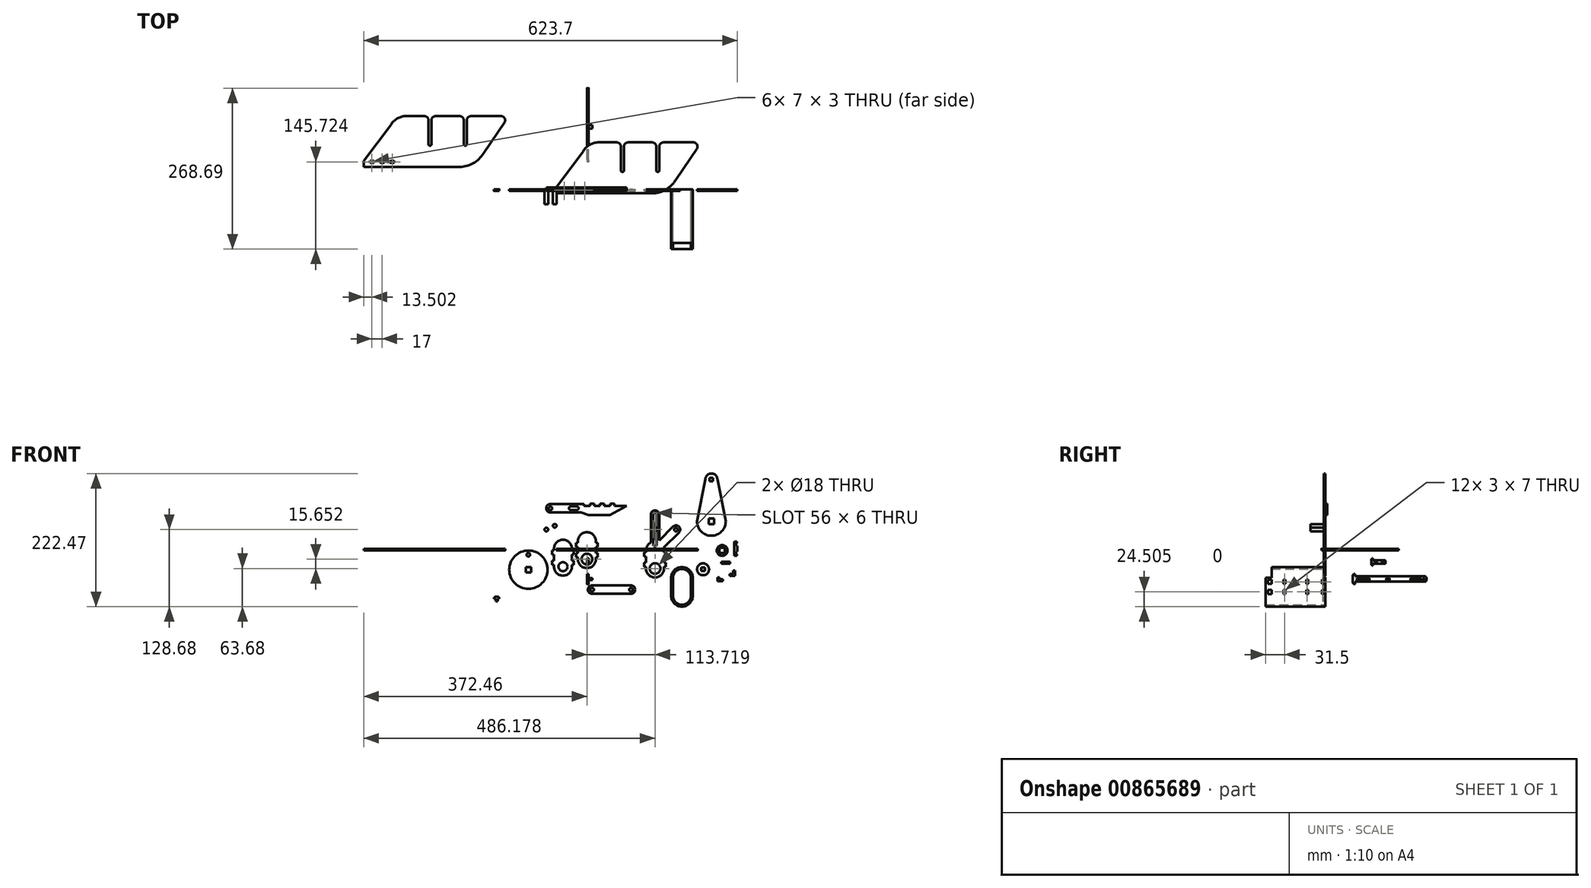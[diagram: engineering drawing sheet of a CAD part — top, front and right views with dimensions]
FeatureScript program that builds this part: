
annotation { "Feature Type Name" : "Feature", "Feature Type Description" : "" }
export const myFeature = defineFeature(function(context is Context, id is Id, definition is map)
    precondition{}
    {
        {
            var Q0;
            Q0=qCreatedBy(makeId("Front.planeOp"),FACE);
            var sketch = newSketch(context, id + "F0", { "sketchPlane" : qUnion([Q0])});
            skLineSegment(sketch, "E0.bottom", {"start": v(-26.86, 73.6) * mm, "end": v(-16.93, 73.6) * mm});
            skLineSegment(sketch, "E0.top", {"start": v(-26.86, 67.6) * mm, "end": v(-16.93, 67.6) * mm});
            skLineSegment(sketch, "E0.right", {"start": v(-16.93, 73.6) * mm, "end": v(-16.93, 67.6) * mm, "construction": true});
            skArc(sketch, "E1", {"start": v(-26.86, 73.6) * mm, "mid": v(-29.93, 70.6) * mm, "end": v(-26.86, 67.6) * mm});
            skArc(sketch, "E2", {"start": v(-16.93, 67.6) * mm, "mid": v(-13.93, 70.6) * mm, "end": v(-16.93, 73.6) * mm});
            skLineSegment(sketch, "E3.bottom", {"start": v(-60.93, 77.6) * mm, "end": v(-9.93, 77.6) * mm});
            skLineSegment(sketch, "E3.top", {"start": v(-60.93, 63.6) * mm, "end": v(-9.93, 63.6) * mm});
            skLineSegment(sketch, "E3.right", {"start": v(-9.93, 77.6) * mm, "end": v(-9.93, 63.6) * mm, "construction": true});
            skArc(sketch, "E4", {"start": v(-60.93, 77.6) * mm, "mid": v(-67.93, 70.6) * mm, "end": v(-60.93, 63.6) * mm});
            skCircle(sketch, "E5", {"center": v(-60.93, 70.6) * mm, "radius": 3 * mm});
            skLineSegment(sketch, "E6", {"start": v(3.07, 59.6) * mm, "end": v(38.07, 59.6) * mm});
            skLineSegment(sketch, "E7", {"start": v(38.07, 59.6) * mm, "end": v(66.07, 74.6) * mm});
            skLineSegment(sketch, "E8", {"start": v(66.07, 74.6) * mm, "end": v(46.07, 74.6) * mm});
            skLineSegment(sketch, "E9", {"start": v(46.07, 74.6) * mm, "end": v(46.07, 78.6) * mm});
            skLineSegment(sketch, "E10", {"start": v(46.07, 78.6) * mm, "end": v(39.07, 78.6) * mm});
            skLineSegment(sketch, "E11", {"start": v(39.07, 78.6) * mm, "end": v(39.07, 74.6) * mm});
            skLineSegment(sketch, "E12", {"start": v(39.07, 74.6) * mm, "end": v(29.07, 74.6) * mm});
            skLineSegment(sketch, "E13", {"start": v(29.07, 74.6) * mm, "end": v(29.07, 78.6) * mm});
            skLineSegment(sketch, "E14", {"start": v(29.07, 78.6) * mm, "end": v(22.07, 78.6) * mm});
            skLineSegment(sketch, "E15", {"start": v(22.07, 78.6) * mm, "end": v(22.07, 74.6) * mm});
            skLineSegment(sketch, "E16", {"start": v(22.07, 74.6) * mm, "end": v(12.07, 74.6) * mm});
            skLineSegment(sketch, "E17", {"start": v(12.07, 74.6) * mm, "end": v(12.07, 78.6) * mm});
            skLineSegment(sketch, "E18", {"start": v(12.07, 78.6) * mm, "end": v(5.07, 78.6) * mm});
            skLineSegment(sketch, "E19", {"start": v(5.07, 78.6) * mm, "end": v(5.07, 74.6) * mm});
            skLineSegment(sketch, "E20", {"start": v(12.07, 78.6) * mm, "end": v(39.07, 78.6) * mm, "construction": true});
            skLineSegment(sketch, "E21", {"start": v(22.07, 74.6) * mm, "end": v(29.07, 74.6) * mm, "construction": true});
            skLineSegment(sketch, "E22", {"start": v(39.07, 74.6) * mm, "end": v(46.07, 74.6) * mm, "construction": true});
            skLineSegment(sketch, "E23", {"start": v(-9.93, 63.6) * mm, "end": v(3.07, 59.6) * mm});
            skLineSegment(sketch, "E24", {"start": v(-9.93, 77.6) * mm, "end": v(-4.93, 77.6) * mm});
            skLineSegment(sketch, "E25", {"start": v(-4.93, 77.6) * mm, "end": v(-4.93, 74.6) * mm});
            skLineSegment(sketch, "E26", {"start": v(-4.93, 74.6) * mm, "end": v(5.07, 74.6) * mm});
            skLineSegment(sketch, "E27", {"start": v(-60.93, 77.6) * mm, "end": v(-60.93, 63.6) * mm, "construction": true});
            skLineSegment(sketch, "E28", {"start": v(-26.86, 73.6) * mm, "end": v(-26.86, 67.6) * mm, "construction": true});
            skSolve(sketch);
        }
        {
            var Q0;
            Q0=qCreatedBy(makeId("Front.planeOp"),FACE);
            var sketch = newSketch(context, id + "F1", { "sketchPlane" : qUnion([Q0])});
            skLineSegment(sketch, "E29", {"start": v(-54.91, 3) * mm, "end": v(-24.91, 3) * mm, "construction": true});
            skCircle(sketch, "E30", {"center": v(-39.91, -27) * mm, "radius": 7.5 * mm});
            skLineSegment(sketch, "E31", {"start": v(-24.91, 3) * mm, "end": v(-24.91, 0) * mm});
            skLineSegment(sketch, "E32", {"start": v(-21.91, 0) * mm, "end": v(-24.91, 0) * mm});
            skLineSegment(sketch, "E33", {"start": v(-21.91, 0) * mm, "end": v(-21.91, -7) * mm});
            skLineSegment(sketch, "E34", {"start": v(-24.91, -7) * mm, "end": v(-21.91, -7) * mm});
            skLineSegment(sketch, "E35", {"start": v(-24.91, -7) * mm, "end": v(-24.91, -17) * mm});
            skLineSegment(sketch, "E36", {"start": v(-21.91, -17) * mm, "end": v(-24.91, -17) * mm});
            skLineSegment(sketch, "E37", {"start": v(-21.91, -17) * mm, "end": v(-21.91, -24) * mm});
            skLineSegment(sketch, "E38", {"start": v(-24.91, -24) * mm, "end": v(-21.91, -24) * mm});
            skLineSegment(sketch, "E39", {"start": v(-24.91, -24) * mm, "end": v(-24.91, -27) * mm});
            skLineSegment(sketch, "E40", {"start": v(-54.91, 3) * mm, "end": v(-54.91, 0) * mm});
            skLineSegment(sketch, "E41", {"start": v(-57.91, 0) * mm, "end": v(-54.91, 0) * mm});
            skLineSegment(sketch, "E42", {"start": v(-57.91, 0) * mm, "end": v(-57.91, -7) * mm});
            skLineSegment(sketch, "E43", {"start": v(-54.91, -7) * mm, "end": v(-57.91, -7) * mm});
            skLineSegment(sketch, "E44", {"start": v(-54.91, -7) * mm, "end": v(-54.91, -17) * mm});
            skLineSegment(sketch, "E45", {"start": v(-57.91, -17) * mm, "end": v(-54.91, -17) * mm});
            skLineSegment(sketch, "E46", {"start": v(-57.91, -17) * mm, "end": v(-57.91, -24) * mm});
            skLineSegment(sketch, "E47", {"start": v(-54.91, -24) * mm, "end": v(-57.91, -24) * mm});
            skLineSegment(sketch, "E48", {"start": v(-54.91, -24) * mm, "end": v(-54.91, -27) * mm});
            skLineSegment(sketch, "E49", {"start": v(-54.91, -27) * mm, "end": v(-24.91, -27) * mm, "construction": true});
            skArc(sketch, "E50", {"start": v(-24.91, 3) * mm, "mid": v(-39.91, 18) * mm, "end": v(-54.91, 3) * mm});
            skArc(sketch, "E51", {"start": v(-54.91, -27) * mm, "mid": v(-39.91, -42) * mm, "end": v(-24.91, -27) * mm});
            skSolve(sketch);
        }
        {
            var Q0;
            Q0=qCreatedBy(makeId("Top.planeOp"),FACE);
            var sketch = newSketch(context, id + "F2", { "sketchPlane" : qUnion([Q0])});
            skLineSegment(sketch, "E52", {"start": v(-51.21, -6.8) * mm, "end": v(108.79, -6.8) * mm});
            skLineSegment(sketch, "E53", {"start": v(148.63, 16.2) * mm, "end": v(183.83, 67.7) * mm});
            skLineSegment(sketch, "E54", {"start": v(-6.21, 63.2) * mm, "end": v(-51.21, 3.2) * mm});
            skLineSegment(sketch, "E55", {"start": v(-51.21, 3.2) * mm, "end": v(-51.21, -6.8) * mm});
            skArc(sketch, "E56", {"start": v(108.79, -6.8) * mm, "mid": v(131.79, -0.64) * mm, "end": v(148.63, 16.2) * mm});
            skLineSegment(sketch, "E57", {"start": v(-41.21, -2.8) * mm, "end": v(-0.21, -2.8) * mm, "construction": true});
            skLineSegment(sketch, "E58", {"start": v(-0.21, -2.8) * mm, "end": v(-0.21, -6.8) * mm, "construction": true});
            skLineSegment(sketch, "E59", {"start": v(-0.21, -2.8) * mm, "end": v(-0.21, 3.2) * mm, "construction": true});
            skLineSegment(sketch, "E60", {"start": v(-0.21, 3.2) * mm, "end": v(-41.21, 3.2) * mm, "construction": true});
            skLineSegment(sketch, "E61", {"start": v(-41.21, 3.2) * mm, "end": v(-41.21, -2.8) * mm, "construction": true});
            skLineSegment(sketch, "E62", {"start": v(-51.21, 3.2) * mm, "end": v(-41.21, 3.2) * mm, "construction": true});
            skLineSegment(sketch, "E63", {"start": v(-51.21, 3.2) * mm, "end": v(-51.21, -96.8) * mm, "construction": true});
            skLineSegment(sketch, "E64", {"start": v(-51.21, -96.8) * mm, "end": v(188.79, -96.8) * mm, "construction": true});
            skLineSegment(sketch, "E65", {"start": v(188.79, -96.8) * mm, "end": v(188.79, 73.46) * mm, "construction": true});
            skLineSegment(sketch, "E66.bottom", {"start": v(-41.21, -2.8) * mm, "end": v(-34.21, -2.8) * mm});
            skLineSegment(sketch, "E66.top", {"start": v(-41.21, 0.2) * mm, "end": v(-34.21, 0.2) * mm});
            skLineSegment(sketch, "E66.left", {"start": v(-41.21, -2.8) * mm, "end": v(-41.21, 0.2) * mm});
            skLineSegment(sketch, "E66.right", {"start": v(-34.21, -2.8) * mm, "end": v(-34.21, 0.2) * mm});
            skLineSegment(sketch, "E67.bottom", {"start": v(-24.21, -2.8) * mm, "end": v(-17.21, -2.8) * mm});
            skLineSegment(sketch, "E67.top", {"start": v(-24.21, 0.2) * mm, "end": v(-17.21, 0.2) * mm});
            skLineSegment(sketch, "E67.left", {"start": v(-24.21, -2.8) * mm, "end": v(-24.21, 0.2) * mm});
            skLineSegment(sketch, "E67.right", {"start": v(-17.21, -2.8) * mm, "end": v(-17.21, 0.2) * mm});
            skLineSegment(sketch, "E68.bottom", {"start": v(-0.21, -2.8) * mm, "end": v(-7.21, -2.8) * mm});
            skLineSegment(sketch, "E68.top", {"start": v(-0.21, 0.2) * mm, "end": v(-7.21, 0.2) * mm});
            skLineSegment(sketch, "E68.left", {"start": v(-0.21, -2.8) * mm, "end": v(-0.21, 0.2) * mm});
            skLineSegment(sketch, "E68.right", {"start": v(-7.21, -2.8) * mm, "end": v(-7.21, 0.2) * mm});
            skLineSegment(sketch, "E69", {"start": v(108.79, 39.2) * mm, "end": v(108.79, -6.8) * mm, "construction": true});
            skLineSegment(sketch, "E70", {"start": v(108.79, 39.2) * mm, "end": v(148.63, 16.2) * mm, "construction": true});
            skArc(sketch, "E71", {"start": v(183.83, 67.7) * mm, "mid": v(183.83, 74.7) * mm, "end": v(177.77, 78.2) * mm});
            skLineSegment(sketch, "E72", {"start": v(177.77, 78.2) * mm, "end": v(177.77, 71.2) * mm, "construction": true});
            skLineSegment(sketch, "E73", {"start": v(183.83, 67.7) * mm, "end": v(177.77, 71.2) * mm, "construction": true});
            skLineSegment(sketch, "E74", {"start": v(177.77, 78.2) * mm, "end": v(127.77, 78.2) * mm});
            skLineSegment(sketch, "E75", {"start": v(120.77, 71.2) * mm, "end": v(120.77, 31.2) * mm});
            skLineSegment(sketch, "E76", {"start": v(115.77, 71.2) * mm, "end": v(115.77, 31.2) * mm});
            skLineSegment(sketch, "E77", {"start": v(61.77, 71.2) * mm, "end": v(61.77, 31.2) * mm});
            skLineSegment(sketch, "E78", {"start": v(56.77, 71.2) * mm, "end": v(56.77, 31.2) * mm});
            skLineSegment(sketch, "E79", {"start": v(19.77, 78.2) * mm, "end": v(49.77, 78.2) * mm});
            skLineSegment(sketch, "E80", {"start": v(68.77, 78.2) * mm, "end": v(108.77, 78.2) * mm});
            skArc(sketch, "E81", {"start": v(127.77, 78.2) * mm, "mid": v(122.82, 76.15) * mm, "end": v(120.77, 71.2) * mm});
            skArc(sketch, "E82", {"start": v(115.77, 71.2) * mm, "mid": v(113.72, 76.15) * mm, "end": v(108.77, 78.2) * mm});
            skArc(sketch, "E83", {"start": v(115.77, 31.2) * mm, "mid": v(118.27, 28.7) * mm, "end": v(120.77, 31.2) * mm});
            skArc(sketch, "E84", {"start": v(68.77, 78.2) * mm, "mid": v(63.82, 76.15) * mm, "end": v(61.77, 71.2) * mm});
            skArc(sketch, "E85", {"start": v(56.77, 71.2) * mm, "mid": v(54.72, 76.15) * mm, "end": v(49.77, 78.2) * mm});
            skArc(sketch, "E86", {"start": v(56.77, 31.2) * mm, "mid": v(59.27, 28.7) * mm, "end": v(61.77, 31.2) * mm});
            skLineSegment(sketch, "E87", {"start": v(127.77, 78.2) * mm, "end": v(127.77, 71.2) * mm, "construction": true});
            skLineSegment(sketch, "E88", {"start": v(120.77, 71.2) * mm, "end": v(127.77, 71.2) * mm, "construction": true});
            skLineSegment(sketch, "E89", {"start": v(108.77, 78.2) * mm, "end": v(108.77, 71.2) * mm, "construction": true});
            skLineSegment(sketch, "E90", {"start": v(115.77, 71.2) * mm, "end": v(108.77, 71.2) * mm, "construction": true});
            skLineSegment(sketch, "E91", {"start": v(120.77, 31.2) * mm, "end": v(115.77, 31.2) * mm, "construction": true});
            skLineSegment(sketch, "E92", {"start": v(61.77, 71.2) * mm, "end": v(68.77, 71.2) * mm, "construction": true});
            skLineSegment(sketch, "E93", {"start": v(68.77, 78.2) * mm, "end": v(68.77, 71.2) * mm, "construction": true});
            skLineSegment(sketch, "E94", {"start": v(49.77, 78.2) * mm, "end": v(49.77, 71.2) * mm, "construction": true});
            skLineSegment(sketch, "E95", {"start": v(56.77, 71.2) * mm, "end": v(49.77, 71.2) * mm, "construction": true});
            skLineSegment(sketch, "E96", {"start": v(56.77, 31.2) * mm, "end": v(61.77, 31.2) * mm, "construction": true});
            skArc(sketch, "E97", {"start": v(19.77, 78.2) * mm, "mid": v(4.77, 74.18) * mm, "end": v(-6.21, 63.2) * mm});
            skLineSegment(sketch, "E98", {"start": v(19.77, 78.2) * mm, "end": v(19.77, 48.2) * mm, "construction": true});
            skLineSegment(sketch, "E99", {"start": v(-6.21, 63.2) * mm, "end": v(19.77, 48.2) * mm, "construction": true});
            skSolve(sketch);
        }
        {
            var Q0;
            Q0=qCreatedBy(makeId("Top.planeOp"),FACE);
            var sketch = newSketch(context, id + "F3", { "sketchPlane" : qUnion([Q0])});
            skLineSegment(sketch, "E100", {"start": v(-372.46, 37.22) * mm, "end": v(-212.46, 37.22) * mm});
            skLineSegment(sketch, "E101", {"start": v(-172.62, 60.22) * mm, "end": v(-137.42, 111.72) * mm});
            skLineSegment(sketch, "E102", {"start": v(-327.46, 107.22) * mm, "end": v(-372.46, 47.22) * mm});
            skLineSegment(sketch, "E103", {"start": v(-372.46, 47.22) * mm, "end": v(-372.46, 37.22) * mm});
            skArc(sketch, "E104", {"start": v(-212.46, 37.22) * mm, "mid": v(-189.46, 43.39) * mm, "end": v(-172.62, 60.22) * mm});
            skLineSegment(sketch, "E105", {"start": v(-362.46, 41.22) * mm, "end": v(-321.46, 41.22) * mm, "construction": true});
            skLineSegment(sketch, "E106", {"start": v(-321.46, 41.22) * mm, "end": v(-321.46, 37.22) * mm, "construction": true});
            skLineSegment(sketch, "E107", {"start": v(-321.46, 41.22) * mm, "end": v(-321.46, 47.22) * mm, "construction": true});
            skLineSegment(sketch, "E108", {"start": v(-321.46, 47.22) * mm, "end": v(-362.46, 47.22) * mm, "construction": true});
            skLineSegment(sketch, "E109", {"start": v(-362.46, 47.22) * mm, "end": v(-362.46, 41.22) * mm, "construction": true});
            skLineSegment(sketch, "E110", {"start": v(-372.46, 47.22) * mm, "end": v(-362.46, 47.22) * mm, "construction": true});
            skLineSegment(sketch, "E111", {"start": v(-372.46, 47.22) * mm, "end": v(-372.46, -2.78) * mm, "construction": true});
            skLineSegment(sketch, "E112", {"start": v(-372.46, -2.78) * mm, "end": v(-132.46, -2.78) * mm, "construction": true});
            skLineSegment(sketch, "E113", {"start": v(-132.46, -2.78) * mm, "end": v(-132.46, 91.24) * mm, "construction": true});
            skLineSegment(sketch, "E114.bottom", {"start": v(-362.46, 47.22) * mm, "end": v(-355.46, 47.22) * mm});
            skLineSegment(sketch, "E114.top", {"start": v(-362.46, 44.22) * mm, "end": v(-355.46, 44.22) * mm});
            skLineSegment(sketch, "E114.left", {"start": v(-362.46, 47.22) * mm, "end": v(-362.46, 44.22) * mm});
            skLineSegment(sketch, "E114.right", {"start": v(-355.46, 47.22) * mm, "end": v(-355.46, 44.22) * mm});
            skLineSegment(sketch, "E115.bottom", {"start": v(-345.46, 47.22) * mm, "end": v(-338.46, 47.22) * mm});
            skLineSegment(sketch, "E115.top", {"start": v(-345.46, 44.22) * mm, "end": v(-338.46, 44.22) * mm});
            skLineSegment(sketch, "E115.left", {"start": v(-345.46, 47.22) * mm, "end": v(-345.46, 44.22) * mm});
            skLineSegment(sketch, "E115.right", {"start": v(-338.46, 47.22) * mm, "end": v(-338.46, 44.22) * mm});
            skLineSegment(sketch, "E116.bottom", {"start": v(-321.46, 47.22) * mm, "end": v(-328.46, 47.22) * mm});
            skLineSegment(sketch, "E116.top", {"start": v(-321.46, 44.22) * mm, "end": v(-328.46, 44.22) * mm});
            skLineSegment(sketch, "E116.left", {"start": v(-321.46, 47.22) * mm, "end": v(-321.46, 44.22) * mm});
            skLineSegment(sketch, "E116.right", {"start": v(-328.46, 47.22) * mm, "end": v(-328.46, 44.22) * mm});
            skLineSegment(sketch, "E117", {"start": v(-212.46, 83.22) * mm, "end": v(-212.46, 37.22) * mm, "construction": true});
            skLineSegment(sketch, "E118", {"start": v(-212.46, 83.22) * mm, "end": v(-172.62, 60.22) * mm, "construction": true});
            skLineSegment(sketch, "E119", {"start": v(-301.48, 122.22) * mm, "end": v(-271.48, 122.22) * mm});
            skLineSegment(sketch, "E120", {"start": v(-264.48, 115.22) * mm, "end": v(-264.48, 75.22) * mm});
            skLineSegment(sketch, "E121", {"start": v(-259.48, 115.22) * mm, "end": v(-259.48, 75.22) * mm});
            skLineSegment(sketch, "E122", {"start": v(-205.48, 115.22) * mm, "end": v(-205.48, 75.22) * mm});
            skLineSegment(sketch, "E123", {"start": v(-200.48, 115.22) * mm, "end": v(-200.48, 75.22) * mm});
            skLineSegment(sketch, "E124", {"start": v(-252.48, 122.22) * mm, "end": v(-212.48, 122.22) * mm});
            skLineSegment(sketch, "E125", {"start": v(-193.48, 122.22) * mm, "end": v(-143.48, 122.22) * mm});
            skArc(sketch, "E126", {"start": v(-137.42, 111.72) * mm, "mid": v(-137.42, 118.72) * mm, "end": v(-143.48, 122.22) * mm});
            skArc(sketch, "E127", {"start": v(-193.48, 122.22) * mm, "mid": v(-198.43, 120.17) * mm, "end": v(-200.48, 115.22) * mm});
            skArc(sketch, "E128", {"start": v(-205.48, 115.22) * mm, "mid": v(-207.53, 120.17) * mm, "end": v(-212.48, 122.22) * mm});
            skArc(sketch, "E129", {"start": v(-205.48, 75.22) * mm, "mid": v(-202.98, 72.72) * mm, "end": v(-200.48, 75.22) * mm});
            skArc(sketch, "E130", {"start": v(-252.48, 122.22) * mm, "mid": v(-257.43, 120.17) * mm, "end": v(-259.48, 115.22) * mm});
            skArc(sketch, "E131", {"start": v(-264.48, 115.22) * mm, "mid": v(-266.53, 120.17) * mm, "end": v(-271.48, 122.22) * mm});
            skArc(sketch, "E132", {"start": v(-264.48, 75.22) * mm, "mid": v(-261.98, 72.72) * mm, "end": v(-259.48, 75.22) * mm});
            skArc(sketch, "E133", {"start": v(-301.48, 122.22) * mm, "mid": v(-316.48, 118.2) * mm, "end": v(-327.46, 107.22) * mm});
            skLineSegment(sketch, "E134", {"start": v(-137.42, 111.72) * mm, "end": v(-143.48, 115.22) * mm, "construction": true});
            skLineSegment(sketch, "E135", {"start": v(-143.48, 122.22) * mm, "end": v(-143.48, 115.22) * mm, "construction": true});
            skLineSegment(sketch, "E136", {"start": v(-200.48, 115.22) * mm, "end": v(-193.48, 115.22) * mm, "construction": true});
            skLineSegment(sketch, "E137", {"start": v(-193.48, 122.22) * mm, "end": v(-193.48, 115.22) * mm, "construction": true});
            skLineSegment(sketch, "E138", {"start": v(-205.48, 115.22) * mm, "end": v(-212.48, 115.22) * mm, "construction": true});
            skLineSegment(sketch, "E139", {"start": v(-212.48, 122.22) * mm, "end": v(-212.48, 115.22) * mm, "construction": true});
            skLineSegment(sketch, "E140", {"start": v(-252.48, 122.22) * mm, "end": v(-252.48, 115.22) * mm, "construction": true});
            skLineSegment(sketch, "E141", {"start": v(-259.48, 115.22) * mm, "end": v(-252.48, 115.22) * mm, "construction": true});
            skLineSegment(sketch, "E142", {"start": v(-264.48, 115.22) * mm, "end": v(-271.48, 115.22) * mm, "construction": true});
            skLineSegment(sketch, "E143", {"start": v(-271.48, 122.22) * mm, "end": v(-271.48, 115.22) * mm, "construction": true});
            skLineSegment(sketch, "E144", {"start": v(-327.46, 107.22) * mm, "end": v(-301.48, 92.22) * mm, "construction": true});
            skLineSegment(sketch, "E145", {"start": v(-301.48, 122.22) * mm, "end": v(-301.48, 92.22) * mm, "construction": true});
            skLineSegment(sketch, "E146", {"start": v(-264.48, 75.22) * mm, "end": v(-259.48, 75.22) * mm, "construction": true});
            skLineSegment(sketch, "E147", {"start": v(-205.48, 75.22) * mm, "end": v(-200.48, 75.22) * mm, "construction": true});
            skSolve(sketch);
        }
        {
            var Q0;
            Q0=makeQuery(id+"F3.imprint","IMPRINT",FACE,{"disambiguationData":[TD([[makeQuery(id+"F3.imprint","IMPRINT",EDGE,{"derivedFrom":sQuery(id+"F3.wireOp",EDGE,"E100")}),1.0]])]});
            extrude(context, id + "F4", {"entities" : qUnion([Q0]), "depth" : 3 * mm, "offsetDistance" : 25 * mm});
        }
        {
            var Q0;
            Q0=makeQuery(id+"F2.imprint","IMPRINT",FACE,{"disambiguationData":[TD([[makeQuery(id+"F2.imprint","IMPRINT",EDGE,{"derivedFrom":sQuery(id+"F2.wireOp",EDGE,"E52")}),1.0]])]});
            extrude(context, id + "F5", {"entities" : qUnion([Q0]), "depth" : 3 * mm, "offsetDistance" : 25 * mm});
        }
        {
            var Q0;
            Q0 = qSketchRegion(id + "F0", true);
            extrude(context, id + "F6", {"entities" : qUnion([Q0]), "depth" : 3 * mm, "offsetDistance" : 25 * mm});
        }
        {
            var Q0;
            Q0 = qSketchRegion(id + "F0", true);
            extrude(context, id + "F7", {"entities" : qUnion([Q0]), "oppositeDirection" : true, "depth" : 3 * mm, "offsetDistance" : 25 * mm});
        }
        {
            var Q0;
            Q0=qCreatedBy(makeId("Front.planeOp"),FACE);
            var sketch = newSketch(context, id + "F8", { "sketchPlane" : qUnion([Q0])});
            skLineSegment(sketch, "E148.bottom", {"start": v(98.72, 0) * mm, "end": v(128.72, 0) * mm, "construction": true});
            skLineSegment(sketch, "E148.top", {"start": v(98.72, -30) * mm, "end": v(128.72, -30) * mm, "construction": true});
            skArc(sketch, "E149", {"start": v(128.72, 0) * mm, "mid": v(113.72, 15) * mm, "end": v(98.72, 0) * mm, "construction": true});
            skLineSegment(sketch, "E150", {"start": v(120.72, 16.9) * mm, "end": v(143.77, 39.95) * mm});
            skLineSegment(sketch, "E151", {"start": v(143.77, 39.95) * mm, "end": v(153.67, 30.05) * mm, "construction": true});
            skLineSegment(sketch, "E152", {"start": v(153.67, 30.05) * mm, "end": v(128.05, 4.43) * mm});
            skLineSegment(sketch, "E153", {"start": v(148.72, 35) * mm, "end": v(113.72, 0) * mm, "construction": true});
            skArc(sketch, "E154", {"start": v(153.67, 30.05) * mm, "mid": v(153.67, 39.95) * mm, "end": v(143.77, 39.95) * mm});
            skCircle(sketch, "E155", {"center": v(148.72, 35) * mm, "radius": 3 * mm});
            skCircle(sketch, "E156", {"center": v(113.72, -30) * mm, "radius": 9 * mm});
            skArc(sketch, "E157", {"start": v(128.05, 4.43) * mm, "mid": v(128.55, 2.24) * mm, "end": v(128.72, 0) * mm});
            skLineSegment(sketch, "E158", {"start": v(128.72, 0) * mm, "end": v(128.72, -3) * mm});
            skLineSegment(sketch, "E159", {"start": v(131.72, -3) * mm, "end": v(128.72, -3) * mm});
            skLineSegment(sketch, "E160", {"start": v(131.72, -3) * mm, "end": v(131.72, -10) * mm});
            skLineSegment(sketch, "E161", {"start": v(128.72, -10) * mm, "end": v(131.72, -10) * mm});
            skLineSegment(sketch, "E162", {"start": v(128.72, -10) * mm, "end": v(128.72, -20) * mm});
            skLineSegment(sketch, "E163", {"start": v(131.72, -20) * mm, "end": v(128.72, -20) * mm});
            skLineSegment(sketch, "E164", {"start": v(131.72, -20) * mm, "end": v(131.72, -27) * mm});
            skLineSegment(sketch, "E165", {"start": v(128.72, -27) * mm, "end": v(131.72, -27) * mm});
            skLineSegment(sketch, "E166", {"start": v(128.72, -27) * mm, "end": v(128.72, -30) * mm});
            skLineSegment(sketch, "E167", {"start": v(98.72, 0) * mm, "end": v(98.72, -3) * mm});
            skLineSegment(sketch, "E168", {"start": v(95.72, -3) * mm, "end": v(98.72, -3) * mm});
            skLineSegment(sketch, "E169", {"start": v(95.72, -3) * mm, "end": v(95.72, -10) * mm});
            skLineSegment(sketch, "E170", {"start": v(98.72, -10) * mm, "end": v(95.72, -10) * mm});
            skLineSegment(sketch, "E171", {"start": v(98.72, -10) * mm, "end": v(98.72, -20) * mm});
            skLineSegment(sketch, "E172", {"start": v(95.72, -20) * mm, "end": v(98.72, -20) * mm});
            skLineSegment(sketch, "E173", {"start": v(95.72, -20) * mm, "end": v(95.72, -27) * mm});
            skLineSegment(sketch, "E174", {"start": v(98.72, -27) * mm, "end": v(95.72, -27) * mm});
            skLineSegment(sketch, "E175", {"start": v(98.72, -27) * mm, "end": v(98.72, -30) * mm});
            skLineSegment(sketch, "E176", {"start": v(109.22, 18.48) * mm, "end": v(99.61, 18.48) * mm, "construction": true});
            skArc(sketch, "E177", {"start": v(106.72, 13.27) * mm, "mid": v(100.87, 7.75) * mm, "end": v(98.72, 0) * mm});
            skLineSegment(sketch, "E178", {"start": v(113.72, 0) * mm, "end": v(113.72, 60) * mm, "construction": true});
            skLineSegment(sketch, "E179", {"start": v(106.72, 60) * mm, "end": v(120.72, 60) * mm, "construction": true});
            skLineSegment(sketch, "E180", {"start": v(120.72, 60) * mm, "end": v(120.72, 16.9) * mm});
            skLineSegment(sketch, "E181", {"start": v(106.72, 60) * mm, "end": v(106.72, 13.27) * mm});
            skArc(sketch, "E182", {"start": v(120.72, 60) * mm, "mid": v(113.72, 67) * mm, "end": v(106.72, 60) * mm});
            skArc(sketch, "E183", {"start": v(116.72, 60) * mm, "mid": v(113.72, 63) * mm, "end": v(110.72, 60) * mm});
            skArc(sketch, "E184", {"start": v(116.72, 10) * mm, "mid": v(113.72, 7) * mm, "end": v(110.72, 10) * mm});
            skLineSegment(sketch, "E185", {"start": v(116.72, 60) * mm, "end": v(116.72, 10) * mm});
            skLineSegment(sketch, "E186", {"start": v(110.72, 60) * mm, "end": v(110.72, 10) * mm});
            skArc(sketch, "E187", {"start": v(98.72, -30) * mm, "mid": v(113.72, -45) * mm, "end": v(128.72, -30) * mm});
            skSolve(sketch);
        }
        {
            var Q0;
            Q0 = qSketchRegion(id + "F8", true);
            extrude(context, id + "F9", {"entities" : qUnion([Q0]), "depth" : 3 * mm, "offsetDistance" : 25 * mm});
        }
        {
            var Q0;
            Q0=qCreatedBy(makeId("Front.planeOp"),FACE);
            var sketch = newSketch(context, id + "F10", { "sketchPlane" : qUnion([Q0])});
            skCircle(sketch, "E188", {"center": v(-67.74, 35.05) * mm, "radius": 3 * mm});
            skSolve(sketch);
        }
        {
            var Q0;
            Q0 = qSketchRegion(id + "F10", true);
            extrude(context, id + "F11", {"entities" : qUnion([Q0]), "depth" : 25 * mm, "offsetDistance" : 25 * mm});
        }
        {
            var Q0;
            Q0=qCreatedBy(makeId("Front.planeOp"),FACE);
            var sketch = newSketch(context, id + "F12", { "sketchPlane" : qUnion([Q0])});
            skCircle(sketch, "E189", {"center": v(-53.73, 41.3) * mm, "radius": 3 * mm});
            skSolve(sketch);
        }
        {
            var Q0;
            Q0=makeQuery(id+"F12.imprint","IMPRINT",FACE,{"disambiguationData":[TD([[makeQuery(id+"F12.imprint","IMPRINT",EDGE,{"derivedFrom":sQuery(id+"F12.wireOp",EDGE,"E189")}),1.0]])]});
            extrude(context, id + "F13", {"entities" : qUnion([Q0]), "depth" : 25 * mm, "offsetDistance" : 25 * mm});
        }
        {
            var Q0;
            Q0=qCreatedBy(makeId("Front.planeOp"),FACE);
            var sketch = newSketch(context, id + "F14", { "sketchPlane" : qUnion([Q0])});
            skCircle(sketch, "E190", {"center": v(-97.63, -32) * mm, "radius": 32 * mm});
            skLineSegment(sketch, "E191", {"start": v(-97.63, -32) * mm, "end": v(-97.63, 0) * mm, "construction": true});
            skCircle(sketch, "E192", {"center": v(-97.63, -7) * mm, "radius": 3 * mm});
            skLineSegment(sketch, "E193.bottom", {"start": v(-93.13, -36.5) * mm, "end": v(-102.13, -36.5) * mm});
            skLineSegment(sketch, "E193.top", {"start": v(-93.13, -27.5) * mm, "end": v(-102.13, -27.5) * mm});
            skLineSegment(sketch, "E193.left", {"start": v(-93.13, -36.5) * mm, "end": v(-93.13, -27.5) * mm});
            skLineSegment(sketch, "E193.right", {"start": v(-102.13, -36.5) * mm, "end": v(-102.13, -27.5) * mm});
            skSolve(sketch);
        }
        {
            var Q0;
            Q0=makeQuery(id+"F14.imprint","IMPRINT",FACE,{"disambiguationData":[TD([[makeQuery(id+"F14.imprint","IMPRINT",EDGE,{"derivedFrom":sQuery(id+"F14.wireOp",EDGE,"E190")}),1.0]])]});
            extrude(context, id + "F15", {"entities" : qUnion([Q0]), "depth" : 3 * mm, "offsetDistance" : 25 * mm});
        }
        {
            var Q0;
            Q0=qCreatedBy(makeId("Front.planeOp"),FACE);
            var sketch = newSketch(context, id + "F16", { "sketchPlane" : qUnion([Q0])});
            skLineSegment(sketch, "E194.bottom", {"start": v(8.64, -58.35) * mm, "end": v(73.64, -58.35) * mm});
            skLineSegment(sketch, "E194.top", {"start": v(8.64, -72.35) * mm, "end": v(73.64, -72.35) * mm});
            skLineSegment(sketch, "E194.left", {"start": v(8.64, -58.35) * mm, "end": v(8.64, -72.35) * mm, "construction": true});
            skLineSegment(sketch, "E194.right", {"start": v(73.64, -58.35) * mm, "end": v(73.64, -72.35) * mm, "construction": true});
            skArc(sketch, "E195", {"start": v(8.64, -58.35) * mm, "mid": v(1.64, -65.35) * mm, "end": v(8.64, -72.35) * mm});
            skArc(sketch, "E196", {"start": v(73.64, -72.35) * mm, "mid": v(80.64, -65.35) * mm, "end": v(73.64, -58.35) * mm});
            skCircle(sketch, "E197", {"center": v(8.64, -65.35) * mm, "radius": 3 * mm});
            skCircle(sketch, "E198", {"center": v(73.64, -65.35) * mm, "radius": 3 * mm});
            skSolve(sketch);
        }
        {
            var Q0;
            Q0=makeQuery(id+"F16.imprint","IMPRINT",FACE,{"disambiguationData":[TD([[makeQuery(id+"F16.imprint","IMPRINT",EDGE,{"derivedFrom":sQuery(id+"F16.wireOp",EDGE,"E194.bottom")}),-1.0]])]});
            extrude(context, id + "F17", {"entities" : qUnion([Q0]), "depth" : 3 * mm, "offsetDistance" : 25 * mm});
        }
        {
            var Q0;
            Q0=qCreatedBy(makeId("Front.planeOp"),FACE);
            var sketch = newSketch(context, id + "F18", { "sketchPlane" : qUnion([Q0])});
            skCircle(sketch, "E199", {"center": v(-45.5, -58.9) * mm, "radius": 10 * mm});
            skSolve(sketch);
        }
        {
            var Q0;
            Q0=makeQuery(id+"F18.imprint","IMPRINT",FACE,{"disambiguationData":[TD([[makeQuery(id+"F18.imprint","IMPRINT",EDGE,{"derivedFrom":sQuery(id+"F18.wireOp",EDGE,"E199")}),1.0]])]});
            extrude(context, id + "F19", {"entities" : qUnion([Q0]), "depth" : 100 * mm, "offsetDistance" : 25 * mm});
        }
        {
            var Q0;
            Q0=qCreatedBy(makeId("Front.planeOp"),FACE);
            var sketch = newSketch(context, id + "F20", { "sketchPlane" : qUnion([Q0])});
            skLineSegment(sketch, "E200.bottom", {"start": v(173.69, -75.68) * mm, "end": v(143.69, -75.68) * mm});
            skLineSegment(sketch, "E200.top", {"start": v(173.69, -45.68) * mm, "end": v(143.69, -45.68) * mm});
            skLineSegment(sketch, "E200.left", {"start": v(173.69, -75.68) * mm, "end": v(173.69, -45.68) * mm});
            skLineSegment(sketch, "E200.right", {"start": v(143.69, -75.68) * mm, "end": v(143.69, -45.68) * mm});
            skPoint(sketch, "E200.middle", {"position": v(158.69, -60.68) * mm});
            skArc(sketch, "E201", {"start": v(173.69, -45.68) * mm, "mid": v(158.69, -30.68) * mm, "end": v(143.69, -45.68) * mm});
            skArc(sketch, "E202", {"start": v(143.69, -75.68) * mm, "mid": v(158.69, -90.68) * mm, "end": v(173.69, -75.68) * mm});
            skLineSegment(sketch, "E203", {"start": v(140.69, -45.68) * mm, "end": v(140.69, -75.68) * mm});
            skLineSegment(sketch, "E204", {"start": v(176.69, -45.68) * mm, "end": v(176.69, -75.68) * mm});
            skArc(sketch, "E205", {"start": v(140.69, -75.68) * mm, "mid": v(158.69, -93.68) * mm, "end": v(176.69, -75.68) * mm});
            skArc(sketch, "E206", {"start": v(176.69, -45.68) * mm, "mid": v(158.69, -27.68) * mm, "end": v(140.69, -45.68) * mm});
            skSolve(sketch);
        }
        {
            var Q0;
            Q0=makeQuery(id+"F20.imprint","IMPRINT",FACE,{"disambiguationData":[TD([[makeQuery(id+"F20.imprint","IMPRINT",EDGE,{"derivedFrom":sQuery(id+"F20.wireOp",EDGE,"E200.left")}),-1.0]])]});
            extrude(context, id + "F21", {"entities" : qUnion([Q0]), "depth" : 100 * mm, "offsetDistance" : 25 * mm});
        }
        {
            var Q0;
            Q0=makeQuery(id+"F21.opExtrude","SWEPT_FACE",FACE,{"disambiguationData":[OSD([sQuery(id+"F20.wireOp",EDGE,"E204")])]});
            var sketch = newSketch(context, id + "F22", { "sketchPlane" : qUnion([Q0])});
            skLineSegment(sketch, "E207", {"start": v(-100, -45.68) * mm, "end": v(-90, -45.68) * mm});
            skLineSegment(sketch, "E208", {"start": v(-90, -45.68) * mm, "end": v(-90, -27.68) * mm});
            skLineSegment(sketch, "E209", {"start": v(-90, -27.68) * mm, "end": v(-100, -27.68) * mm});
            skLineSegment(sketch, "E210", {"start": v(-100, -45.68) * mm, "end": v(-100, -27.68) * mm});
            skLineSegment(sketch, "E211.bottom", {"start": v(-90, -55.68) * mm, "end": v(-96, -55.68) * mm});
            skLineSegment(sketch, "E211.top", {"start": v(-90, -48.68) * mm, "end": v(-96, -48.68) * mm});
            skLineSegment(sketch, "E211.left", {"start": v(-90, -55.68) * mm, "end": v(-90, -48.68) * mm});
            skLineSegment(sketch, "E211.right", {"start": v(-96, -55.68) * mm, "end": v(-96, -48.68) * mm});
            skPoint(sketch, "E211.middle", {"position": v(-93, -52.18) * mm});
            skLineSegment(sketch, "E212.bottom", {"start": v(-90, -72.68) * mm, "end": v(-96, -72.68) * mm});
            skLineSegment(sketch, "E212.top", {"start": v(-90, -65.68) * mm, "end": v(-96, -65.68) * mm});
            skLineSegment(sketch, "E212.left", {"start": v(-90, -72.68) * mm, "end": v(-90, -65.68) * mm});
            skLineSegment(sketch, "E212.right", {"start": v(-96, -72.68) * mm, "end": v(-96, -65.68) * mm});
            skPoint(sketch, "E212.middle", {"position": v(-93, -69.18) * mm});
            skLineSegment(sketch, "E213.bottom", {"start": v(-3, -55.68) * mm, "end": v(-6, -55.68) * mm});
            skLineSegment(sketch, "E213.top", {"start": v(-3, -48.68) * mm, "end": v(-6, -48.68) * mm});
            skLineSegment(sketch, "E213.left", {"start": v(-3, -55.68) * mm, "end": v(-3, -48.68) * mm});
            skLineSegment(sketch, "E213.right", {"start": v(-6, -55.68) * mm, "end": v(-6, -48.68) * mm});
            skPoint(sketch, "E213.middle", {"position": v(-4.5, -52.18) * mm});
            skLineSegment(sketch, "E214.bottom", {"start": v(-3, -72.68) * mm, "end": v(-6, -72.68) * mm});
            skLineSegment(sketch, "E214.top", {"start": v(-3, -65.68) * mm, "end": v(-6, -65.68) * mm});
            skLineSegment(sketch, "E214.left", {"start": v(-3, -72.68) * mm, "end": v(-3, -65.68) * mm});
            skLineSegment(sketch, "E214.right", {"start": v(-6, -72.68) * mm, "end": v(-6, -65.68) * mm});
            skPoint(sketch, "E214.middle", {"position": v(-4.5, -69.18) * mm});
            skLineSegment(sketch, "E215.bottom", {"start": v(-67, -55.68) * mm, "end": v(-70, -55.68) * mm});
            skLineSegment(sketch, "E215.top", {"start": v(-67, -48.68) * mm, "end": v(-70, -48.68) * mm});
            skLineSegment(sketch, "E215.left", {"start": v(-67, -55.68) * mm, "end": v(-67, -48.68) * mm});
            skLineSegment(sketch, "E215.right", {"start": v(-70, -55.68) * mm, "end": v(-70, -48.68) * mm});
            skPoint(sketch, "E215.middle", {"position": v(-68.5, -52.18) * mm});
            skLineSegment(sketch, "E216.bottom", {"start": v(-29, -55.68) * mm, "end": v(-32, -55.68) * mm});
            skLineSegment(sketch, "E216.top", {"start": v(-29, -48.68) * mm, "end": v(-32, -48.68) * mm});
            skLineSegment(sketch, "E216.left", {"start": v(-29, -55.68) * mm, "end": v(-29, -48.68) * mm});
            skLineSegment(sketch, "E216.right", {"start": v(-32, -55.68) * mm, "end": v(-32, -48.68) * mm});
            skPoint(sketch, "E216.middle", {"position": v(-30.5, -52.18) * mm});
            skLineSegment(sketch, "E217.bottom", {"start": v(-67, -72.68) * mm, "end": v(-70, -72.68) * mm});
            skLineSegment(sketch, "E217.top", {"start": v(-67, -65.68) * mm, "end": v(-70, -65.68) * mm});
            skLineSegment(sketch, "E217.left", {"start": v(-67, -72.68) * mm, "end": v(-67, -65.68) * mm});
            skLineSegment(sketch, "E217.right", {"start": v(-70, -72.68) * mm, "end": v(-70, -65.68) * mm});
            skPoint(sketch, "E217.middle", {"position": v(-68.5, -69.18) * mm});
            skLineSegment(sketch, "E218.bottom", {"start": v(-29, -72.68) * mm, "end": v(-32, -72.68) * mm});
            skLineSegment(sketch, "E218.top", {"start": v(-29, -65.68) * mm, "end": v(-32, -65.68) * mm});
            skLineSegment(sketch, "E218.left", {"start": v(-29, -72.68) * mm, "end": v(-29, -65.68) * mm});
            skLineSegment(sketch, "E218.right", {"start": v(-32, -72.68) * mm, "end": v(-32, -65.68) * mm});
            skPoint(sketch, "E218.middle", {"position": v(-30.5, -69.18) * mm});
            skSolve(sketch);
        }
        {
            var Q0;
            Q0 = qSketchRegion(id + "F22", true);
            extrude(context, id + "F23", {"entities" : qUnion([Q0]), "operationType" : NewBodyOperationType.REMOVE, "endBound" : BoundingType.THROUGH_ALL, "oppositeDirection" : true, "depth" : 25 * mm, "offsetDistance" : 25 * mm});
        }
        {
            var Q0;
            Q0=qCreatedBy(makeId("Front.planeOp"),FACE);
            var sketch = newSketch(context, id + "F24", { "sketchPlane" : qUnion([Q0])});
            skLineSegment(sketch, "E219", {"start": v(-15, 15.65) * mm, "end": v(15, 15.65) * mm, "construction": true});
            skCircle(sketch, "E220", {"center": v(0, -14.35) * mm, "radius": 9 * mm});
            skLineSegment(sketch, "E221", {"start": v(15, 15.65) * mm, "end": v(15, 12.65) * mm});
            skLineSegment(sketch, "E222", {"start": v(18, 12.65) * mm, "end": v(15, 12.65) * mm});
            skLineSegment(sketch, "E223", {"start": v(18, 12.65) * mm, "end": v(18, 5.65) * mm});
            skLineSegment(sketch, "E224", {"start": v(15, 5.65) * mm, "end": v(18, 5.65) * mm});
            skLineSegment(sketch, "E225", {"start": v(15, 5.65) * mm, "end": v(15, -4.35) * mm});
            skLineSegment(sketch, "E226", {"start": v(18, -4.35) * mm, "end": v(15, -4.35) * mm});
            skLineSegment(sketch, "E227", {"start": v(18, -4.35) * mm, "end": v(18, -11.35) * mm});
            skLineSegment(sketch, "E228", {"start": v(15, -11.35) * mm, "end": v(18, -11.35) * mm});
            skLineSegment(sketch, "E229", {"start": v(15, -11.35) * mm, "end": v(15, -14.35) * mm});
            skLineSegment(sketch, "E230", {"start": v(-15, 15.65) * mm, "end": v(-15, 12.65) * mm});
            skLineSegment(sketch, "E231", {"start": v(-18, 12.65) * mm, "end": v(-15, 12.65) * mm});
            skLineSegment(sketch, "E232", {"start": v(-18, 12.65) * mm, "end": v(-18, 5.65) * mm});
            skLineSegment(sketch, "E233", {"start": v(-15, 5.65) * mm, "end": v(-18, 5.65) * mm});
            skLineSegment(sketch, "E234", {"start": v(-15, 5.65) * mm, "end": v(-15, -4.35) * mm});
            skLineSegment(sketch, "E235", {"start": v(-18, -4.35) * mm, "end": v(-15, -4.35) * mm});
            skLineSegment(sketch, "E236", {"start": v(-18, -4.35) * mm, "end": v(-18, -11.35) * mm});
            skLineSegment(sketch, "E237", {"start": v(-15, -11.35) * mm, "end": v(-18, -11.35) * mm});
            skLineSegment(sketch, "E238", {"start": v(-15, -11.35) * mm, "end": v(-15, -14.35) * mm});
            skLineSegment(sketch, "E239", {"start": v(-15, -14.35) * mm, "end": v(15, -14.35) * mm, "construction": true});
            skArc(sketch, "E240", {"start": v(15, 15.65) * mm, "mid": v(0, 30.65) * mm, "end": v(-15, 15.65) * mm});
            skArc(sketch, "E241", {"start": v(-15, -14.35) * mm, "mid": v(0, -29.35) * mm, "end": v(15, -14.35) * mm});
            skSolve(sketch);
        }
        {
            var Q0;
            Q0 = qSketchRegion(id + "F24", true);
            extrude(context, id + "F25", {"entities" : qUnion([Q0]), "depth" : 3 * mm, "offsetDistance" : 25 * mm});
        }
        {
            var Q0;
            Q0=makeQuery(id+"F1.imprint","IMPRINT",FACE,{"disambiguationData":[TD([[makeQuery(id+"F1.imprint","IMPRINT",EDGE,{"derivedFrom":sQuery(id+"F1.wireOp",EDGE,"E30")}),-1.0]])]});
            extrude(context, id + "F26", {"entities" : qUnion([Q0]), "depth" : 3 * mm, "offsetDistance" : 25 * mm});
        }
        {
            var Q0;
            Q0=qCreatedBy(makeId("Right.planeOp"),FACE);
            var sketch = newSketch(context, id + "F27", { "sketchPlane" : qUnion([Q0])});
            skLineSegment(sketch, "E242.bottom", {"start": v(49.19, -43.05) * mm, "end": v(168.69, -43.05) * mm});
            skLineSegment(sketch, "E242.top", {"start": v(49.19, -52.05) * mm, "end": v(168.69, -52.05) * mm});
            skLineSegment(sketch, "E242.left", {"start": v(49.19, -43.05) * mm, "end": v(49.19, -52.05) * mm, "construction": true});
            skLineSegment(sketch, "E242.right", {"start": v(168.69, -43.05) * mm, "end": v(168.69, -52.05) * mm});
            skLineSegment(sketch, "E243", {"start": v(49.19, -43.05) * mm, "end": v(49.19, -39.05) * mm});
            skLineSegment(sketch, "E244", {"start": v(45.19, -43.05) * mm, "end": v(45.19, -52.05) * mm});
            skLineSegment(sketch, "E245", {"start": v(49.19, -56.05) * mm, "end": v(49.19, -52.05) * mm});
            skArc(sketch, "E246", {"start": v(49.19, -39.05) * mm, "mid": v(46.36, -40.22) * mm, "end": v(45.19, -43.05) * mm});
            skArc(sketch, "E247", {"start": v(49.19, -56.05) * mm, "mid": v(46.36, -54.88) * mm, "end": v(45.19, -52.05) * mm});
            skLineSegment(sketch, "E248.bottom", {"start": v(52.19, -46.05) * mm, "end": v(73.19, -46.05) * mm});
            skLineSegment(sketch, "E248.top", {"start": v(52.19, -49.05) * mm, "end": v(73.19, -49.05) * mm});
            skLineSegment(sketch, "E248.left", {"start": v(52.19, -46.05) * mm, "end": v(52.19, -49.05) * mm});
            skLineSegment(sketch, "E248.right", {"start": v(73.19, -46.05) * mm, "end": v(73.19, -49.05) * mm});
            skLineSegment(sketch, "E249.bottom", {"start": v(141.69, -46.05) * mm, "end": v(159.69, -46.05) * mm});
            skLineSegment(sketch, "E249.top", {"start": v(141.69, -49.05) * mm, "end": v(159.69, -49.05) * mm});
            skLineSegment(sketch, "E249.left", {"start": v(141.69, -46.05) * mm, "end": v(141.69, -49.05) * mm});
            skLineSegment(sketch, "E249.right", {"start": v(159.69, -46.05) * mm, "end": v(159.69, -49.05) * mm});
            skLineSegment(sketch, "E250.bottom", {"start": v(107.19, -49.05) * mm, "end": v(101.19, -49.05) * mm});
            skLineSegment(sketch, "E250.top", {"start": v(107.19, -46.05) * mm, "end": v(101.19, -46.05) * mm});
            skLineSegment(sketch, "E250.left", {"start": v(107.19, -49.05) * mm, "end": v(107.19, -46.05) * mm});
            skLineSegment(sketch, "E250.right", {"start": v(101.19, -49.05) * mm, "end": v(101.19, -46.05) * mm});
            skPoint(sketch, "E250.middle", {"position": v(104.19, -47.55) * mm});
            skLineSegment(sketch, "E251.bottom", {"start": v(162.69, -46.05) * mm, "end": v(165.69, -46.05) * mm});
            skLineSegment(sketch, "E251.top", {"start": v(162.69, -49.05) * mm, "end": v(165.69, -49.05) * mm});
            skLineSegment(sketch, "E251.left", {"start": v(162.69, -46.05) * mm, "end": v(162.69, -49.05) * mm});
            skLineSegment(sketch, "E251.right", {"start": v(165.69, -46.05) * mm, "end": v(165.69, -49.05) * mm});
            skSolve(sketch);
        }
        {
            var Q0;
            Q0=makeQuery(id+"F27.imprint","IMPRINT",FACE,{"disambiguationData":[TD([[makeQuery(id+"F27.imprint","IMPRINT",EDGE,{"derivedFrom":sQuery(id+"F27.wireOp",EDGE,"E242.bottom")}),-1.0]])]});
            extrude(context, id + "F28", {"entities" : qUnion([Q0]), "depth" : 3 * mm, "offsetDistance" : 25 * mm});
        }
        {
            var Q0;
            Q0=makeQuery(id+"F28.opExtrude","SWEPT_EDGE",EDGE,{"disambiguationData":[OSD([sQuery(id+"F27.wireOp",EDGE,"E242.bottom"),sQuery(id+"F27.wireOp",EDGE,"E242.right")])]});
            var Q1;
            Q1=makeQuery(id+"F28.opExtrude","SWEPT_EDGE",EDGE,{"disambiguationData":[OSD([sQuery(id+"F27.wireOp",EDGE,"E242.top"),sQuery(id+"F27.wireOp",EDGE,"E242.right")])]});
            fillet(context, id + "F29", {"entities" : qUnion([Q0, Q1]), "radius" : 3 * mm, "tangentPropagation" : true, "allowEdgeOverflow" : false});
        }
        {
            var Q0;
            Q0=qCreatedBy(makeId("Front.planeOp"),FACE);
            var sketch = newSketch(context, id + "F30", { "sketchPlane" : qUnion([Q0])});
            skLineSegment(sketch, "E252", {"start": v(207.77, 118.8) * mm, "end": v(207.77, 48.8) * mm, "construction": true});
            skLineSegment(sketch, "E253.bottom", {"start": v(212.27, 44.3) * mm, "end": v(203.27, 44.3) * mm});
            skLineSegment(sketch, "E253.top", {"start": v(212.27, 53.3) * mm, "end": v(203.27, 53.3) * mm});
            skLineSegment(sketch, "E253.left", {"start": v(212.27, 44.3) * mm, "end": v(212.27, 53.3) * mm});
            skLineSegment(sketch, "E253.right", {"start": v(203.27, 44.3) * mm, "end": v(203.27, 53.3) * mm});
            skPoint(sketch, "E253.middle", {"position": v(207.77, 48.8) * mm});
            skArc(sketch, "E254", {"start": v(183.77, 48.8) * mm, "mid": v(207.77, 24.8) * mm, "end": v(231.77, 48.8) * mm});
            skLineSegment(sketch, "E255.bottom", {"start": v(210.77, 115.8) * mm, "end": v(204.77, 115.8) * mm});
            skLineSegment(sketch, "E255.top", {"start": v(210.77, 121.8) * mm, "end": v(204.77, 121.8) * mm});
            skLineSegment(sketch, "E255.left", {"start": v(210.77, 115.8) * mm, "end": v(210.77, 121.8) * mm});
            skLineSegment(sketch, "E255.right", {"start": v(204.77, 115.8) * mm, "end": v(204.77, 121.8) * mm});
            skPoint(sketch, "E255.middle", {"position": v(207.77, 118.8) * mm});
            skArc(sketch, "E256", {"start": v(217.77, 118.8) * mm, "mid": v(207.77, 128.8) * mm, "end": v(197.77, 118.8) * mm});
            skLineSegment(sketch, "E257", {"start": v(197.77, 118.8) * mm, "end": v(183.77, 48.8) * mm});
            skLineSegment(sketch, "E258", {"start": v(231.77, 48.8) * mm, "end": v(217.77, 118.8) * mm});
            skSolve(sketch);
        }
        {
            var Q0;
            Q0=makeQuery(id+"F30.imprint","IMPRINT",FACE,{"disambiguationData":[TD([[makeQuery(id+"F30.imprint","IMPRINT",EDGE,{"derivedFrom":sQuery(id+"F30.wireOp",EDGE,"E253.bottom")}),1.0]])]});
            extrude(context, id + "F31", {"entities" : qUnion([Q0]), "depth" : 3 * mm, "offsetDistance" : 25 * mm});
        }
        {
            var Q0;
            Q0=qCreatedBy(makeId("Front.planeOp"),FACE);
            var sketch = newSketch(context, id + "F32", { "sketchPlane" : qUnion([Q0])});
            skCircle(sketch, "E259", {"center": v(225.87, 0) * mm, "radius": 9 * mm});
            skLineSegment(sketch, "E260.bottom", {"start": v(230.37, -4.5) * mm, "end": v(221.37, -4.5) * mm});
            skLineSegment(sketch, "E260.top", {"start": v(230.37, 4.5) * mm, "end": v(221.37, 4.5) * mm});
            skLineSegment(sketch, "E260.left", {"start": v(230.37, -4.5) * mm, "end": v(230.37, 4.5) * mm});
            skLineSegment(sketch, "E260.right", {"start": v(221.37, -4.5) * mm, "end": v(221.37, 4.5) * mm});
            skSolve(sketch);
        }
        {
            var Q0;
            Q0=makeQuery(id+"F32.imprint","IMPRINT",FACE,{"disambiguationData":[TD([[makeQuery(id+"F32.imprint","IMPRINT",EDGE,{"derivedFrom":sQuery(id+"F32.wireOp",EDGE,"E259")}),1.0]])]});
            extrude(context, id + "F33", {"entities" : qUnion([Q0]), "depth" : 3 * mm, "offsetDistance" : 25 * mm});
        }
        {
            var Q0;
            Q0=qCreatedBy(makeId("Front.planeOp"),FACE);
            var sketch = newSketch(context, id + "F34", { "sketchPlane" : qUnion([Q0])});
            skLineSegment(sketch, "E261", {"start": v(249.24, 12.1) * mm, "end": v(249.24, 7.6) * mm});
            skLineSegment(sketch, "E262", {"start": v(249.24, 7.6) * mm, "end": v(251.24, 7.6) * mm});
            skLineSegment(sketch, "E263", {"start": v(251.24, 7.6) * mm, "end": v(251.24, -1.4) * mm});
            skLineSegment(sketch, "E264", {"start": v(251.24, -1.4) * mm, "end": v(249.24, -1.4) * mm});
            skLineSegment(sketch, "E265", {"start": v(249.24, -1.4) * mm, "end": v(249.24, -5.9) * mm});
            skLineSegment(sketch, "E266", {"start": v(249.24, -5.9) * mm, "end": v(250.24, -5.9) * mm});
            skLineSegment(sketch, "E267", {"start": v(250.24, -5.9) * mm, "end": v(250.24, -8.9) * mm});
            skLineSegment(sketch, "E268", {"start": v(250.24, -8.9) * mm, "end": v(246.24, -8.9) * mm});
            skLineSegment(sketch, "E269", {"start": v(246.24, -8.9) * mm, "end": v(246.24, 15.1) * mm});
            skLineSegment(sketch, "E270", {"start": v(246.24, 15.1) * mm, "end": v(250.24, 15.1) * mm});
            skLineSegment(sketch, "E271", {"start": v(250.24, 15.1) * mm, "end": v(250.24, 12.1) * mm});
            skLineSegment(sketch, "E272", {"start": v(250.24, 12.1) * mm, "end": v(249.24, 12.1) * mm});
            skSolve(sketch);
        }
        {
            var Q0;
            Q0=makeQuery(id+"F34.imprint","IMPRINT",FACE,{"disambiguationData":[TD([[makeQuery(id+"F34.imprint","IMPRINT",EDGE,{"derivedFrom":sQuery(id+"F34.wireOp",EDGE,"E261")}),-1.0]])]});
            extrude(context, id + "F35", {"entities" : qUnion([Q0]), "depth" : 3 * mm, "offsetDistance" : 25 * mm});
        }
        {
            var Q0;
            Q0=makeQuery(id+"F27.imprint","IMPRINT",FACE,{"disambiguationData":[TD([[makeQuery(id+"F27.imprint","IMPRINT",EDGE,{"derivedFrom":sQuery(id+"F27.wireOp",EDGE,"E250.bottom")}),-1.0]])]});
            extrude(context, id + "F36", {"entities" : qUnion([Q0]), "depth" : 9 * mm, "offsetDistance" : 25 * mm});
        }
        {
            var Q0;
            Q0=qCreatedBy(makeId("Front.planeOp"),FACE);
            var sketch = newSketch(context, id + "F37", { "sketchPlane" : qUnion([Q0])});
            skLineSegment(sketch, "E273", {"start": v(-152.17, -80.3) * mm, "end": v(-152.17, -84.8) * mm});
            skLineSegment(sketch, "E274", {"start": v(-152.17, -84.8) * mm, "end": v(-149.17, -84.8) * mm});
            skLineSegment(sketch, "E275", {"start": v(-149.17, -84.8) * mm, "end": v(-149.17, -80.3) * mm});
            skLineSegment(sketch, "E276", {"start": v(-149.17, -80.3) * mm, "end": v(-146.17, -80.3) * mm});
            skLineSegment(sketch, "E277", {"start": v(-152.17, -80.3) * mm, "end": v(-155.17, -80.3) * mm});
            skLineSegment(sketch, "E278", {"start": v(-152.17, -77.3) * mm, "end": v(-149.17, -77.3) * mm});
            skArc(sketch, "E279", {"start": v(-155.17, -80.3) * mm, "mid": v(-154.29, -78.18) * mm, "end": v(-152.17, -77.3) * mm});
            skArc(sketch, "E280", {"start": v(-146.17, -80.3) * mm, "mid": v(-147.04, -78.18) * mm, "end": v(-149.17, -77.3) * mm});
            skSolve(sketch);
        }
        {
            var Q0;
            Q0=makeQuery(id+"F37.imprint","IMPRINT",FACE,{"disambiguationData":[TD([[makeQuery(id+"F37.imprint","IMPRINT",EDGE,{"derivedFrom":sQuery(id+"F37.wireOp",EDGE,"E273")}),1.0]])]});
            extrude(context, id + "F38", {"entities" : qUnion([Q0]), "depth" : 3 * mm, "offsetDistance" : 25 * mm});
        }
        {
            var Q0;
            Q0=makeQuery(id+"F19.opExtrude","SWEPT_BODY",BODY,{"disambiguationData":[OSD([sQuery(id+"F18.wireOp",EDGE,"E199")])]});
            deleteBodies(context, id + "F39", {"entities" : qUnion([Q0])});
        }
        {
            var Q0;
            Q0=qCreatedBy(makeId("Right.planeOp"),FACE);
            var sketch = newSketch(context, id + "F40", { "sketchPlane" : qUnion([Q0])});
            skLineSegment(sketch, "E281", {"start": v(79.32, -13.17) * mm, "end": v(79.32, -16.17) * mm});
            skLineSegment(sketch, "E282", {"start": v(79.32, -16.17) * mm, "end": v(98.82, -16.17) * mm});
            skLineSegment(sketch, "E283", {"start": v(100.32, -17.67) * mm, "end": v(100.32, -20.67) * mm});
            skLineSegment(sketch, "E284", {"start": v(98.82, -22.17) * mm, "end": v(79.32, -22.17) * mm});
            skLineSegment(sketch, "E285", {"start": v(79.32, -22.17) * mm, "end": v(79.32, -25.17) * mm});
            skArc(sketch, "E286", {"start": v(79.32, -25.17) * mm, "mid": v(77.2, -24.3) * mm, "end": v(76.32, -22.17) * mm});
            skArc(sketch, "E287", {"start": v(79.32, -13.17) * mm, "mid": v(77.2, -14.05) * mm, "end": v(76.32, -16.17) * mm});
            skLineSegment(sketch, "E288", {"start": v(76.32, -16.17) * mm, "end": v(76.32, -22.17) * mm});
            skLineSegment(sketch, "E289.bottom", {"start": v(85.32, -17.67) * mm, "end": v(82.32, -17.67) * mm});
            skLineSegment(sketch, "E289.top", {"start": v(85.32, -20.67) * mm, "end": v(82.32, -20.67) * mm});
            skLineSegment(sketch, "E289.left", {"start": v(85.32, -17.67) * mm, "end": v(85.32, -20.67) * mm});
            skLineSegment(sketch, "E289.right", {"start": v(82.32, -17.67) * mm, "end": v(82.32, -20.67) * mm});
            skPoint(sketch, "E289.middle", {"position": v(83.82, -19.17) * mm});
            skLineSegment(sketch, "E290", {"start": v(76.32, -19.17) * mm, "end": v(100.32, -19.17) * mm, "construction": true});
            skLineSegment(sketch, "E291.bottom", {"start": v(97.32, -20.67) * mm, "end": v(94.32, -20.67) * mm});
            skLineSegment(sketch, "E291.top", {"start": v(97.32, -17.67) * mm, "end": v(94.32, -17.67) * mm});
            skLineSegment(sketch, "E291.left", {"start": v(97.32, -20.67) * mm, "end": v(97.32, -17.67) * mm});
            skLineSegment(sketch, "E291.right", {"start": v(94.32, -20.67) * mm, "end": v(94.32, -17.67) * mm});
            skPoint(sketch, "E291.middle", {"position": v(95.82, -19.17) * mm});
            skArc(sketch, "E292", {"start": v(100.32, -17.67) * mm, "mid": v(99.88, -16.61) * mm, "end": v(98.82, -16.17) * mm});
            skArc(sketch, "E293", {"start": v(98.82, -22.17) * mm, "mid": v(99.88, -21.74) * mm, "end": v(100.32, -20.67) * mm});
            skSolve(sketch);
        }
        {
            var Q0;
            Q0=makeQuery(id+"F40.imprint","IMPRINT",FACE,{"disambiguationData":[TD([[makeQuery(id+"F40.imprint","IMPRINT",EDGE,{"derivedFrom":sQuery(id+"F40.wireOp",EDGE,"E281")}),-1.0]])]});
            extrude(context, id + "F41", {"entities" : qUnion([Q0]), "depth" : 3 * mm, "offsetDistance" : 25 * mm});
        }
        {
            var Q0;
            Q0=qCreatedBy(makeId("Front.planeOp"),FACE);
            var sketch = newSketch(context, id + "F42", { "sketchPlane" : qUnion([Q0])});
            skLineSegment(sketch, "E294", {"start": v(218.13, -45.08) * mm, "end": v(218.13, -51.08) * mm});
            skLineSegment(sketch, "E295", {"start": v(218.13, -51.08) * mm, "end": v(227.13, -51.08) * mm});
            skLineSegment(sketch, "E296", {"start": v(227.13, -51.08) * mm, "end": v(227.13, -48.08) * mm});
            skLineSegment(sketch, "E297", {"start": v(227.13, -48.08) * mm, "end": v(221.13, -48.08) * mm});
            skLineSegment(sketch, "E298", {"start": v(221.13, -48.08) * mm, "end": v(221.13, -45.08) * mm});
            skLineSegment(sketch, "E299", {"start": v(221.13, -45.08) * mm, "end": v(218.13, -45.08) * mm});
            skSolve(sketch);
        }
        {
            var Q0;
            Q0 = qSketchRegion(id + "F42", true);
            extrude(context, id + "F43", {"entities" : qUnion([Q0]), "depth" : 3 * mm, "offsetDistance" : 25 * mm});
        }
        {
            var Q0;
            Q0=qCreatedBy(makeId("Front.planeOp"),FACE);
            var sketch = newSketch(context, id + "F44", { "sketchPlane" : qUnion([Q0])});
            skLineSegment(sketch, "E300", {"start": v(238.12, -42.3) * mm, "end": v(247.12, -42.3) * mm});
            skLineSegment(sketch, "E301", {"start": v(247.12, -42.3) * mm, "end": v(247.12, -33.3) * mm});
            skLineSegment(sketch, "E302", {"start": v(247.12, -33.3) * mm, "end": v(244.12, -33.3) * mm});
            skLineSegment(sketch, "E303", {"start": v(244.12, -33.3) * mm, "end": v(244.12, -39.3) * mm});
            skLineSegment(sketch, "E304", {"start": v(244.12, -39.3) * mm, "end": v(238.12, -39.3) * mm});
            skLineSegment(sketch, "E305", {"start": v(238.12, -39.3) * mm, "end": v(238.12, -42.3) * mm});
            skSolve(sketch);
        }
        {
            var Q0;
            Q0 = qSketchRegion(id + "F44", true);
            extrude(context, id + "F45", {"entities" : qUnion([Q0]), "depth" : 3 * mm, "offsetDistance" : 25 * mm});
        }
        {
            var Q0;
            Q0=qCreatedBy(makeId("Front.planeOp"),FACE);
            var sketch = newSketch(context, id + "F46", { "sketchPlane" : qUnion([Q0])});
            skLineSegment(sketch, "E306.bottom", {"start": v(239.26, -21.74) * mm, "end": v(224.26, -21.74) * mm});
            skLineSegment(sketch, "E306.top", {"start": v(239.26, -18.74) * mm, "end": v(224.26, -18.74) * mm});
            skLineSegment(sketch, "E306.left", {"start": v(239.26, -21.74) * mm, "end": v(239.26, -18.74) * mm});
            skLineSegment(sketch, "E306.right", {"start": v(224.26, -21.74) * mm, "end": v(224.26, -18.74) * mm});
            skPoint(sketch, "E306.middle", {"position": v(231.76, -20.24) * mm});
            skSolve(sketch);
        }
        {
            var Q0;
            Q0 = qSketchRegion(id + "F46", true);
            extrude(context, id + "F47", {"entities" : qUnion([Q0]), "depth" : 3 * mm, "offsetDistance" : 25 * mm});
        }
        {
            var Q0;
            Q0=qCreatedBy(makeId("Front.planeOp"),FACE);
            var sketch = newSketch(context, id + "F48", { "sketchPlane" : qUnion([Q0])});
            skCircle(sketch, "E307", {"center": v(193.92, -31.33) * mm, "radius": 10 * mm});
            skLineSegment(sketch, "E308.bottom", {"start": v(196.92, -34.33) * mm, "end": v(190.92, -34.33) * mm});
            skLineSegment(sketch, "E308.top", {"start": v(196.92, -28.33) * mm, "end": v(190.92, -28.33) * mm});
            skLineSegment(sketch, "E308.left", {"start": v(196.92, -34.33) * mm, "end": v(196.92, -28.33) * mm});
            skLineSegment(sketch, "E308.right", {"start": v(190.92, -34.33) * mm, "end": v(190.92, -28.33) * mm});
            skSolve(sketch);
        }
        {
            var Q0;
            Q0=makeQuery(id+"F48.imprint","IMPRINT",FACE,{"disambiguationData":[TD([[makeQuery(id+"F48.imprint","IMPRINT",EDGE,{"derivedFrom":sQuery(id+"F48.wireOp",EDGE,"z0m0eXWy-FuTL-irGf-Etuv-9sNHnEFKxXlE")}),-1.0]])]});
            var Q1;
            Q1=makeQuery(id+"F48.imprint","IMPRINT",FACE,{"disambiguationData":[TD([[makeQuery(id+"F48.imprint","IMPRINT",EDGE,{"derivedFrom":sQuery(id+"F48.wireOp",EDGE,"E307")}),1.0]])]});
            extrude(context, id + "F49", {"entities" : qUnion([Q0, Q1]), "depth" : 3 * mm, "offsetDistance" : 25 * mm});
        }
    });
